# Revit family: Wicslide_160_1_leaf_1_track_with_fixed_ligh
name_source: partatom
category: Doors
revit_build: Autodesk Revit Architecture 2014 (Build: 20130308_1515(x64)
units: mm (PartAtom-declared; Revit-internal decimal feet)

## types (1)
- Wicslide_160_1_leaf_1_track_with_fixed_ligh
    Acoustic = Rw (C;Cu)= 47 (-1;-4)dB
    Analytic Construction = <None>
    Assembly Code = B2030110
    Bottom Offset = 45 mm  [stored 0.147638 ft]
    Corrosion Resistance of the Fittings = Class 5
    Date of publishing = 3/14/2015
    Description = The new WICSLIDE 160 lifting sliding system combines excellent thermal insulation with highest functionality and design. Impressive leaf dimensions and enduring operation comfort are your guarantors for maximum customer satisfaction. With state-of-the-art technology and innovative advantages in fabrication WICSLIDE 160 is a high-tech product that sets new standards.
    Design country = Germany
    Door 1 width = 1396 mm
    Door Offset = 19 mm  [stored 0.062336 ft]
    EN1627 Burglar Resistance = RC1N, RC2N, RC2, RC3, SBD
    Edition number = 1
    Frame 1940019 = Yes
    Frame Depth = 160 mm  [stored 0.524934 ft]
    Frame Material = WICONA - Aluminium - RAL7016 - Anthracite Grey - Matt
    Frame Width = 67 mm
    Frame Width 2 = 55 mm
    Frame Width 3 = 43 mm
    Function = Interior
    Glass Material = WICONA -  Glass
    Glass Offset 1 = 138 mm
    Glass Offset 2 = 37 mm  [stored 0.121391 ft]
    Handle Material = Aluminium
    Height = 2100 mm
    Keynote = L20/520
    Leaf Material = WICONA - Aluminium - RAL7016 - Anthracite Grey - Matt
    Load Bearing Capacity of Safety Devices = Fulfilled
    Manufacturer = Wicona
    Manufacturer country = Germany
    Manufacturer name = Wicona
    Material main = Aluminium
    Material secondary = Glass
    Maximum Sash Weight = 160kg as standard design, heavier weights can easily be customised
    Mechanical Strength = Class 4
    Model = Wicslide 160
    Nominal height = 341300
    Nominal width = 323500
    Operating Forces = Class 1
    Operation = IFC_DOORSLIDING
    Product Guid = 0afd48ae-a14c-4f29-91d5-9573b3650314
    Product SKU = WICSLIDE_160_W
    Product data url = http://bimobject.com
    Product family = Windows & Doors
    Product group = Windows
    QR code = http://bimobject.com
    Quality Assurance = Certified according to ISO 9001:2008
    Repeated Opening/Closing = Class 3 (20,000 Cycles)
    Resistance to wind load = Class C3
    Type Comments = Stand Alone
    URL = http://www.wicona.com
    Uniclass2 = Ss-25-30-20-77
    Vent Frame 1940037 & 1040010 = Yes
    Vent Frame 1940037 & 1940041 = No
    Wall Closure = By host
    Watertightness = E1350A
    Weight Net (Kg) = 0
    Width = 3000 mm  [stored 9.84252 ft]

note: [stored X ft] marks values corroborated as IEEE doubles in the binary element streams (Revit-internal decimal feet)

## geometry (parser evidence)
native form markers: Blend x4, Sweep x10
no freeform markers — native parametric forms only
